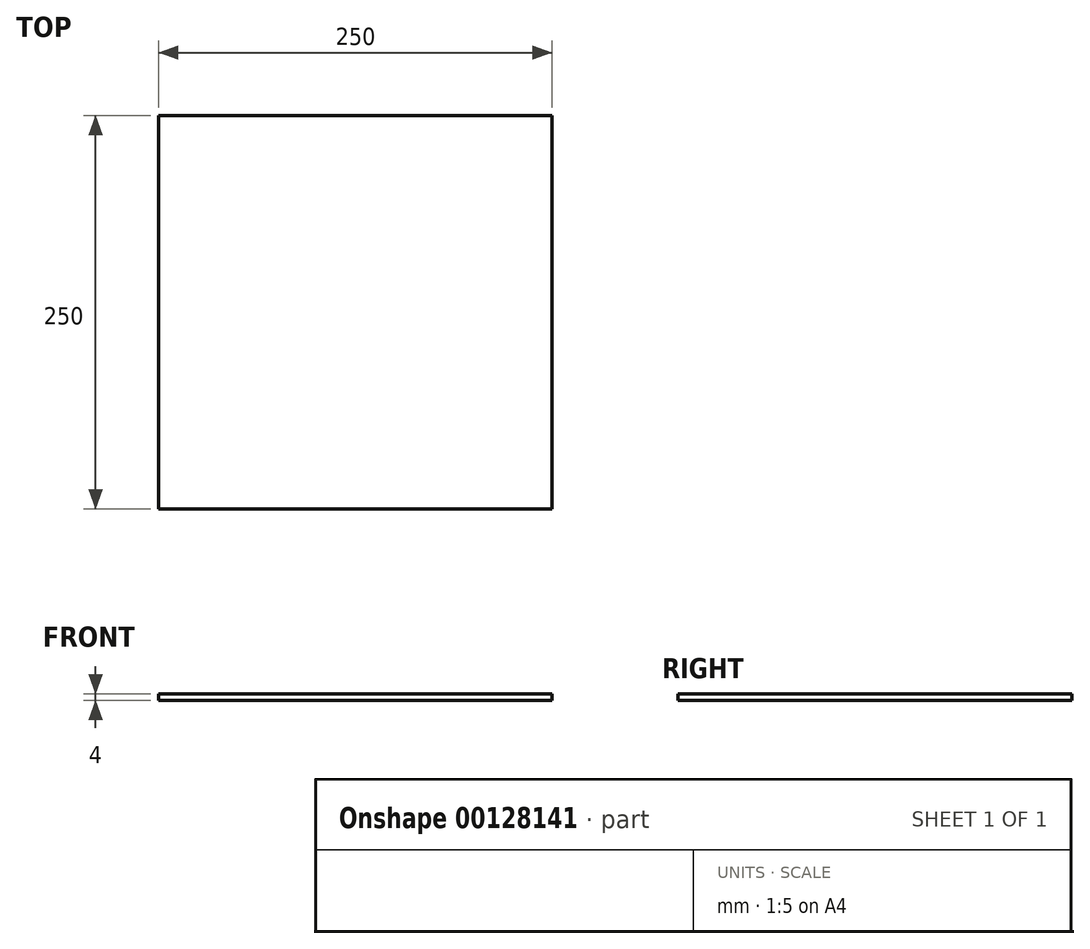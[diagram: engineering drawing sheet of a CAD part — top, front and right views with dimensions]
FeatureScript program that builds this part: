
annotation { "Feature Type Name" : "Feature", "Feature Type Description" : "" }
export const myFeature = defineFeature(function(context is Context, id is Id, definition is map)
    precondition{}
    {
        {
            var Q0;
            Q0=qCreatedBy(makeId("Top.planeOp"),FACE);
            var sketch = newSketch(context, id + "F0", { "sketchPlane" : qUnion([Q0])});
            skLineSegment(sketch, "E0.bottom", {"start": v(0, 0) * mm, "end": v(250, 0) * mm});
            skLineSegment(sketch, "E0.top", {"start": v(0, 250) * mm, "end": v(250, 250) * mm});
            skLineSegment(sketch, "E0.left", {"start": v(0, 0) * mm, "end": v(0, 250) * mm});
            skLineSegment(sketch, "E0.right", {"start": v(250, 0) * mm, "end": v(250, 250) * mm});
            skSolve(sketch);
        }
        {
            var Q0;
            Q0 = qSketchRegion(id + "F0", true);
            extrude(context, id + "F1", {"entities" : qUnion([Q0]), "depth" : 4 * mm});
        }
    });
